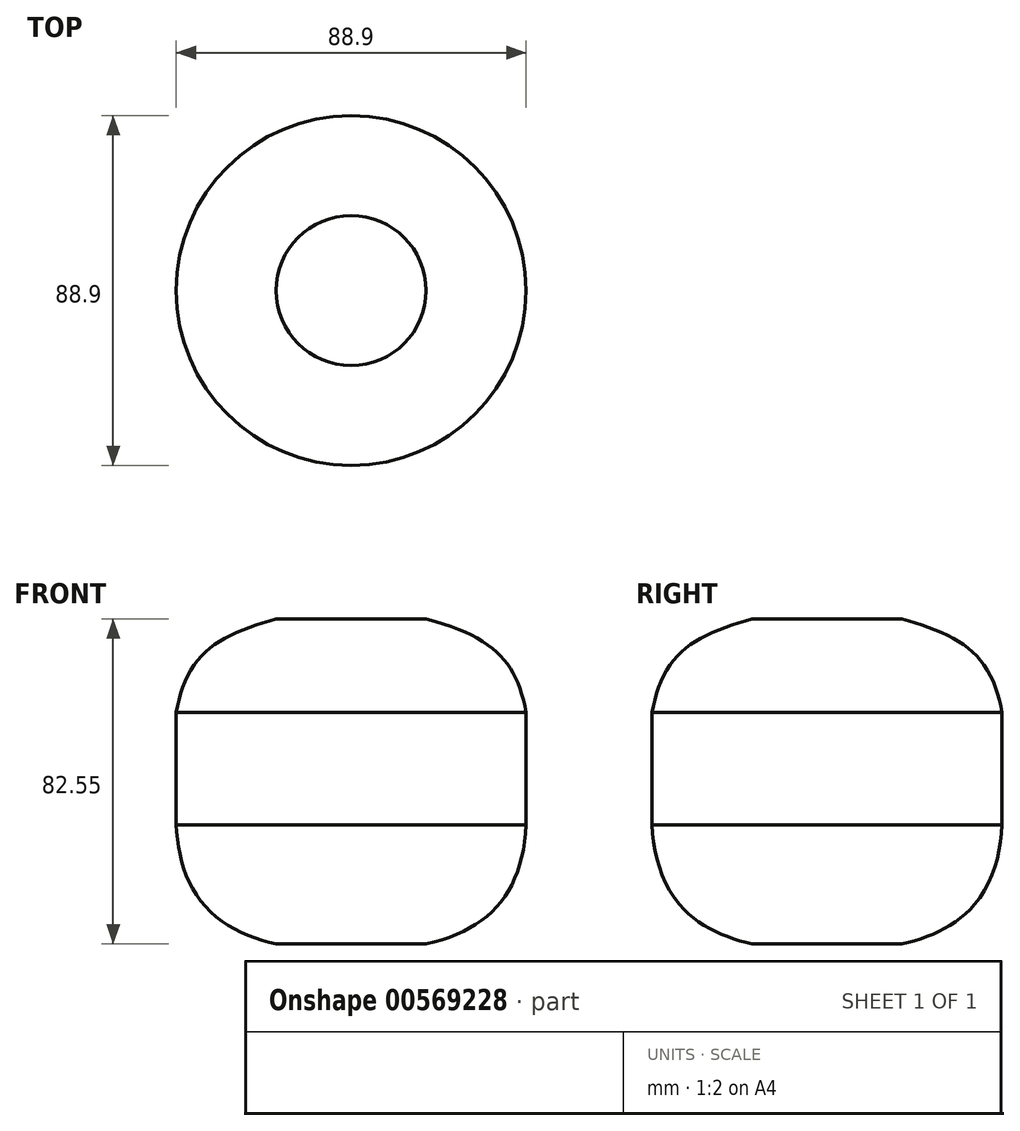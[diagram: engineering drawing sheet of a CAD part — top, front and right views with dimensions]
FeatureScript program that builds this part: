
annotation { "Feature Type Name" : "Feature", "Feature Type Description" : "" }
export const myFeature = defineFeature(function(context is Context, id is Id, definition is map)
    precondition{}
    {
        {
            var Q0;
            Q0=qCreatedBy(makeId("Front.planeOp"),FACE);
            var sketch = newSketch(context, id + "F0", { "sketchPlane" : qUnion([Q0])});
            skLineSegment(sketch, "E0", {"start": v(0, 37.99) * mm, "end": v(0, -44.56) * mm});
            skLineSegment(sketch, "E1.bottom", {"start": v(0, -14.28) * mm, "end": v(44.45, -14.28) * mm});
            skLineSegment(sketch, "E1.top", {"start": v(0, 14.3) * mm, "end": v(44.45, 14.3) * mm});
            skLineSegment(sketch, "E1.left", {"start": v(0, -14.28) * mm, "end": v(0, 14.3) * mm});
            skLineSegment(sketch, "E1.right", {"start": v(44.45, -14.28) * mm, "end": v(44.45, 14.3) * mm});
            skLineSegment(sketch, "E2", {"start": v(0, 37.99) * mm, "end": v(19.05, 37.99) * mm});
            skFitSpline(sketch, "E3", {"points": [v(19.05, 37.99) * mm, v(44.45, 14.3) * mm], "startDerivative": vector(53.16, -14.11) * mm, "endDerivative": vector(7.37, -38.13) * mm});
            skLineSegment(sketch, "E4", {"start": v(0, -44.56) * mm, "end": v(19.05, -44.56) * mm});
            skFitSpline(sketch, "E5", {"points": [v(19.05, -44.56) * mm, v(44.45, -14.28) * mm], "startDerivative": vector(48.45, 10.9) * mm, "endDerivative": vector(2.66, 51.74) * mm});
            skSolve(sketch);
        }
        {
            var Q0;
            Q0=makeQuery(id+"F0.imprint","IMPRINT",FACE,{"disambiguationData":[TD([[makeQuery(id+"F0.imprint","IMPRINT",EDGE,{"derivedFrom":sQuery(id+"F0.wireOp",EDGE,"E1.bottom")}),1.0]])]});
            var Q1;
            Q1=sQuery(id+"F0.wireOp",EDGE,"E0");
            revolve(context, id + "F1", {"entities" : qUnion([Q0]), "axis" : qUnion([Q1]), "revolveType" : RevolveType.FULL});
        }
        {
            var Q0;
            {var subQ2=sQuery(id+"F0.wireOp",EDGE,"E1.bottom");Q0=makeQuery(id+"F0.imprint","IMPRINT",FACE,{"disambiguationData":[TD([[makeQuery(id+"F0.imprint","IMPRINT",EDGE,{"derivedFrom":subQ2}),-1.0]])]});}
            var Q1;
            Q1=sQuery(id+"F0.wireOp",EDGE,"E0");
            revolve(context, id + "F2", {"operationType" : NewBodyOperationType.ADD, "entities" : qUnion([Q0]), "axis" : qUnion([Q1]), "revolveType" : RevolveType.FULL});
        }
        {
            var Q0;
            {var subQ2=sQuery(id+"F0.wireOp",EDGE,"E1.top");Q0=makeQuery(id+"F0.imprint","IMPRINT",FACE,{"disambiguationData":[TD([[makeQuery(id+"F0.imprint","IMPRINT",EDGE,{"derivedFrom":subQ2}),1.0]])]});}
            var Q1;
            Q1=makeQuery(id+"F2.opRevolve","SWEPT_FACE",FACE,{"disambiguationData":[OSD([sQuery(id+"F0.wireOp",EDGE,"E5")])]});
            revolve(context, id + "F3", {"operationType" : NewBodyOperationType.ADD, "entities" : qUnion([Q0]), "axis" : qUnion([Q1]), "revolveType" : RevolveType.FULL});
        }
    });
